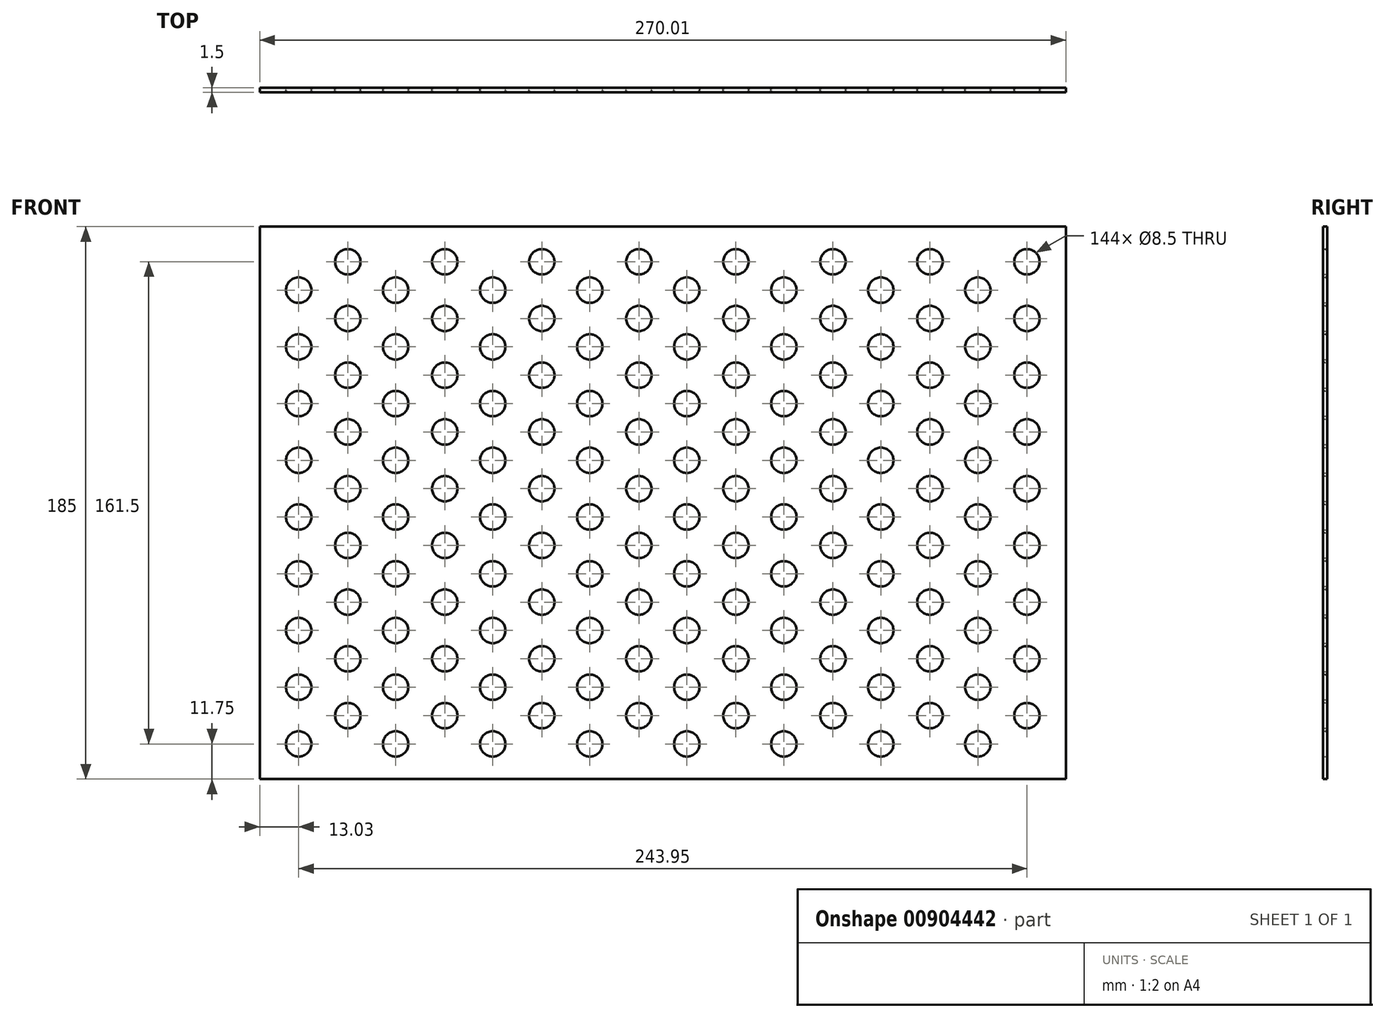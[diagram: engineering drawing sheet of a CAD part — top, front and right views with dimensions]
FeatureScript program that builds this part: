
annotation { "Feature Type Name" : "Feature", "Feature Type Description" : "" }
export const myFeature = defineFeature(function(context is Context, id is Id, definition is map)
    precondition{}
    {
        {
            var Q0;
            Q0=qCreatedBy(makeId("Front.planeOp"),FACE);
            var sketch = newSketch(context, id + "F0", { "sketchPlane" : qUnion([Q0])});
            skCircle(sketch, "E0", {"center": v(0, 0) * mm, "radius": 4.25 * mm});
            skCircle(sketch, "E1", {"center": v(16.45, 9.5) * mm, "radius": 4.25 * mm});
            skCircle(sketch, "E2.0.1.0", {"center": v(0, 19) * mm, "radius": 4.25 * mm});
            skCircle(sketch, "E2.0.1.1", {"center": v(16.45, 28.5) * mm, "radius": 4.25 * mm});
            skCircle(sketch, "E2.0.2.0", {"center": v(0, 38) * mm, "radius": 4.25 * mm});
            skCircle(sketch, "E2.0.2.1", {"center": v(16.45, 47.5) * mm, "radius": 4.25 * mm});
            skCircle(sketch, "E2.0.3.0", {"center": v(0, 57) * mm, "radius": 4.25 * mm});
            skCircle(sketch, "E2.0.3.1", {"center": v(16.45, 66.5) * mm, "radius": 4.25 * mm});
            skCircle(sketch, "E2.0.4.0", {"center": v(0, 76) * mm, "radius": 4.25 * mm});
            skCircle(sketch, "E2.0.4.1", {"center": v(16.45, 85.5) * mm, "radius": 4.25 * mm});
            skCircle(sketch, "E2.0.5.0", {"center": v(0, 95) * mm, "radius": 4.25 * mm});
            skCircle(sketch, "E2.0.5.1", {"center": v(16.45, 104.5) * mm, "radius": 4.25 * mm});
            skCircle(sketch, "E2.0.6.0", {"center": v(0, 114) * mm, "radius": 4.25 * mm});
            skCircle(sketch, "E2.0.6.1", {"center": v(16.45, 123.5) * mm, "radius": 4.25 * mm});
            skCircle(sketch, "E2.0.7.0", {"center": v(0, 133) * mm, "radius": 4.25 * mm});
            skCircle(sketch, "E2.0.7.1", {"center": v(16.45, 142.5) * mm, "radius": 4.25 * mm});
            skCircle(sketch, "E2.0.8.0", {"center": v(0, 152) * mm, "radius": 4.25 * mm});
            skCircle(sketch, "E2.0.8.1", {"center": v(16.45, 161.5) * mm, "radius": 4.25 * mm});
            skCircle(sketch, "E2.1.0.0", {"center": v(32.5, 0) * mm, "radius": 4.25 * mm});
            skCircle(sketch, "E2.1.0.1", {"center": v(48.95, 9.5) * mm, "radius": 4.25 * mm});
            skCircle(sketch, "E2.1.1.0", {"center": v(32.5, 19) * mm, "radius": 4.25 * mm});
            skCircle(sketch, "E2.1.1.1", {"center": v(48.95, 28.5) * mm, "radius": 4.25 * mm});
            skCircle(sketch, "E2.1.2.0", {"center": v(32.5, 38) * mm, "radius": 4.25 * mm});
            skCircle(sketch, "E2.1.2.1", {"center": v(48.95, 47.5) * mm, "radius": 4.25 * mm});
            skCircle(sketch, "E2.1.3.0", {"center": v(32.5, 57) * mm, "radius": 4.25 * mm});
            skCircle(sketch, "E2.1.3.1", {"center": v(48.95, 66.5) * mm, "radius": 4.25 * mm});
            skCircle(sketch, "E2.1.4.0", {"center": v(32.5, 76) * mm, "radius": 4.25 * mm});
            skCircle(sketch, "E2.1.4.1", {"center": v(48.95, 85.5) * mm, "radius": 4.25 * mm});
            skCircle(sketch, "E2.1.5.0", {"center": v(32.5, 95) * mm, "radius": 4.25 * mm});
            skCircle(sketch, "E2.1.5.1", {"center": v(48.95, 104.5) * mm, "radius": 4.25 * mm});
            skCircle(sketch, "E2.1.6.0", {"center": v(32.5, 114) * mm, "radius": 4.25 * mm});
            skCircle(sketch, "E2.1.6.1", {"center": v(48.95, 123.5) * mm, "radius": 4.25 * mm});
            skCircle(sketch, "E2.1.7.0", {"center": v(32.5, 133) * mm, "radius": 4.25 * mm});
            skCircle(sketch, "E2.1.7.1", {"center": v(48.95, 142.5) * mm, "radius": 4.25 * mm});
            skCircle(sketch, "E2.1.8.0", {"center": v(32.5, 152) * mm, "radius": 4.25 * mm});
            skCircle(sketch, "E2.1.8.1", {"center": v(48.95, 161.5) * mm, "radius": 4.25 * mm});
            skCircle(sketch, "E2.2.0.0", {"center": v(65, 0) * mm, "radius": 4.25 * mm});
            skCircle(sketch, "E2.2.0.1", {"center": v(81.45, 9.5) * mm, "radius": 4.25 * mm});
            skCircle(sketch, "E2.2.1.0", {"center": v(65, 19) * mm, "radius": 4.25 * mm});
            skCircle(sketch, "E2.2.1.1", {"center": v(81.45, 28.5) * mm, "radius": 4.25 * mm});
            skCircle(sketch, "E2.2.2.0", {"center": v(65, 38) * mm, "radius": 4.25 * mm});
            skCircle(sketch, "E2.2.2.1", {"center": v(81.45, 47.5) * mm, "radius": 4.25 * mm});
            skCircle(sketch, "E2.2.3.0", {"center": v(65, 57) * mm, "radius": 4.25 * mm});
            skCircle(sketch, "E2.2.3.1", {"center": v(81.45, 66.5) * mm, "radius": 4.25 * mm});
            skCircle(sketch, "E2.2.4.0", {"center": v(65, 76) * mm, "radius": 4.25 * mm});
            skCircle(sketch, "E2.2.4.1", {"center": v(81.45, 85.5) * mm, "radius": 4.25 * mm});
            skCircle(sketch, "E2.2.5.0", {"center": v(65, 95) * mm, "radius": 4.25 * mm});
            skCircle(sketch, "E2.2.5.1", {"center": v(81.45, 104.5) * mm, "radius": 4.25 * mm});
            skCircle(sketch, "E2.2.6.0", {"center": v(65, 114) * mm, "radius": 4.25 * mm});
            skCircle(sketch, "E2.2.6.1", {"center": v(81.45, 123.5) * mm, "radius": 4.25 * mm});
            skCircle(sketch, "E2.2.7.0", {"center": v(65, 133) * mm, "radius": 4.25 * mm});
            skCircle(sketch, "E2.2.7.1", {"center": v(81.45, 142.5) * mm, "radius": 4.25 * mm});
            skCircle(sketch, "E2.2.8.0", {"center": v(65, 152) * mm, "radius": 4.25 * mm});
            skCircle(sketch, "E2.2.8.1", {"center": v(81.45, 161.5) * mm, "radius": 4.25 * mm});
            skLineSegment(sketch, "E2.direction1", {"start": v(0, 0) * mm, "end": v(32.5, 0) * mm, "construction": true});
            skLineSegment(sketch, "E2.direction2", {"start": v(0, 0) * mm, "end": v(0, 19) * mm, "construction": true});
            skCircle(sketch, "E3.0.3.0", {"center": v(97.5, 0) * mm, "radius": 4.25 * mm});
            skCircle(sketch, "E3.2.3.0", {"center": v(113.95, 9.5) * mm, "radius": 4.25 * mm});
            skCircle(sketch, "E3.0.3.1", {"center": v(97.5, 19) * mm, "radius": 4.25 * mm});
            skCircle(sketch, "E3.2.3.1", {"center": v(113.95, 28.5) * mm, "radius": 4.25 * mm});
            skCircle(sketch, "E3.0.3.2", {"center": v(97.5, 38) * mm, "radius": 4.25 * mm});
            skCircle(sketch, "E3.2.3.2", {"center": v(113.95, 47.5) * mm, "radius": 4.25 * mm});
            skCircle(sketch, "E3.0.3.3", {"center": v(97.5, 57) * mm, "radius": 4.25 * mm});
            skCircle(sketch, "E3.2.3.3", {"center": v(113.95, 66.5) * mm, "radius": 4.25 * mm});
            skCircle(sketch, "E3.0.3.4", {"center": v(97.5, 76) * mm, "radius": 4.25 * mm});
            skCircle(sketch, "E3.2.3.4", {"center": v(113.95, 85.5) * mm, "radius": 4.25 * mm});
            skCircle(sketch, "E3.0.3.5", {"center": v(97.5, 95) * mm, "radius": 4.25 * mm});
            skCircle(sketch, "E3.2.3.5", {"center": v(113.95, 104.5) * mm, "radius": 4.25 * mm});
            skCircle(sketch, "E3.0.3.6", {"center": v(97.5, 114) * mm, "radius": 4.25 * mm});
            skCircle(sketch, "E3.2.3.6", {"center": v(113.95, 123.5) * mm, "radius": 4.25 * mm});
            skCircle(sketch, "E3.0.3.7", {"center": v(97.5, 133) * mm, "radius": 4.25 * mm});
            skCircle(sketch, "E3.2.3.7", {"center": v(113.95, 142.5) * mm, "radius": 4.25 * mm});
            skCircle(sketch, "E3.0.3.8", {"center": v(97.5, 152) * mm, "radius": 4.25 * mm});
            skCircle(sketch, "E3.2.3.8", {"center": v(113.95, 161.5) * mm, "radius": 4.25 * mm});
            skCircle(sketch, "E3.0.4.0", {"center": v(130, 0) * mm, "radius": 4.25 * mm});
            skCircle(sketch, "E3.2.4.0", {"center": v(146.45, 9.5) * mm, "radius": 4.25 * mm});
            skCircle(sketch, "E3.0.4.1", {"center": v(130, 19) * mm, "radius": 4.25 * mm});
            skCircle(sketch, "E3.2.4.1", {"center": v(146.45, 28.5) * mm, "radius": 4.25 * mm});
            skCircle(sketch, "E3.0.4.2", {"center": v(130, 38) * mm, "radius": 4.25 * mm});
            skCircle(sketch, "E3.2.4.2", {"center": v(146.45, 47.5) * mm, "radius": 4.25 * mm});
            skCircle(sketch, "E3.0.4.3", {"center": v(130, 57) * mm, "radius": 4.25 * mm});
            skCircle(sketch, "E3.2.4.3", {"center": v(146.45, 66.5) * mm, "radius": 4.25 * mm});
            skCircle(sketch, "E3.0.4.4", {"center": v(130, 76) * mm, "radius": 4.25 * mm});
            skCircle(sketch, "E3.2.4.4", {"center": v(146.45, 85.5) * mm, "radius": 4.25 * mm});
            skCircle(sketch, "E3.0.4.5", {"center": v(130, 95) * mm, "radius": 4.25 * mm});
            skCircle(sketch, "E3.2.4.5", {"center": v(146.45, 104.5) * mm, "radius": 4.25 * mm});
            skCircle(sketch, "E3.0.4.6", {"center": v(130, 114) * mm, "radius": 4.25 * mm});
            skCircle(sketch, "E3.2.4.6", {"center": v(146.45, 123.5) * mm, "radius": 4.25 * mm});
            skCircle(sketch, "E3.0.4.7", {"center": v(130, 133) * mm, "radius": 4.25 * mm});
            skCircle(sketch, "E3.2.4.7", {"center": v(146.45, 142.5) * mm, "radius": 4.25 * mm});
            skCircle(sketch, "E3.0.4.8", {"center": v(130, 152) * mm, "radius": 4.25 * mm});
            skCircle(sketch, "E3.2.4.8", {"center": v(146.45, 161.5) * mm, "radius": 4.25 * mm});
            skCircle(sketch, "E3.0.5.0", {"center": v(162.5, 0) * mm, "radius": 4.25 * mm});
            skCircle(sketch, "E3.2.5.0", {"center": v(178.95, 9.5) * mm, "radius": 4.25 * mm});
            skCircle(sketch, "E3.0.5.1", {"center": v(162.5, 19) * mm, "radius": 4.25 * mm});
            skCircle(sketch, "E3.2.5.1", {"center": v(178.95, 28.5) * mm, "radius": 4.25 * mm});
            skCircle(sketch, "E3.0.5.2", {"center": v(162.5, 38) * mm, "radius": 4.25 * mm});
            skCircle(sketch, "E3.2.5.2", {"center": v(178.95, 47.5) * mm, "radius": 4.25 * mm});
            skCircle(sketch, "E3.0.5.3", {"center": v(162.5, 57) * mm, "radius": 4.25 * mm});
            skCircle(sketch, "E3.2.5.3", {"center": v(178.95, 66.5) * mm, "radius": 4.25 * mm});
            skCircle(sketch, "E3.0.5.4", {"center": v(162.5, 76) * mm, "radius": 4.25 * mm});
            skCircle(sketch, "E3.2.5.4", {"center": v(178.95, 85.5) * mm, "radius": 4.25 * mm});
            skCircle(sketch, "E3.0.5.5", {"center": v(162.5, 95) * mm, "radius": 4.25 * mm});
            skCircle(sketch, "E3.2.5.5", {"center": v(178.95, 104.5) * mm, "radius": 4.25 * mm});
            skCircle(sketch, "E3.0.5.6", {"center": v(162.5, 114) * mm, "radius": 4.25 * mm});
            skCircle(sketch, "E3.2.5.6", {"center": v(178.95, 123.5) * mm, "radius": 4.25 * mm});
            skCircle(sketch, "E3.0.5.7", {"center": v(162.5, 133) * mm, "radius": 4.25 * mm});
            skCircle(sketch, "E3.2.5.7", {"center": v(178.95, 142.5) * mm, "radius": 4.25 * mm});
            skCircle(sketch, "E3.0.5.8", {"center": v(162.5, 152) * mm, "radius": 4.25 * mm});
            skCircle(sketch, "E3.2.5.8", {"center": v(178.95, 161.5) * mm, "radius": 4.25 * mm});
            skCircle(sketch, "E3.0.6.0", {"center": v(195, 0) * mm, "radius": 4.25 * mm});
            skCircle(sketch, "E3.2.6.0", {"center": v(211.45, 9.5) * mm, "radius": 4.25 * mm});
            skCircle(sketch, "E3.0.6.1", {"center": v(195, 19) * mm, "radius": 4.25 * mm});
            skCircle(sketch, "E3.2.6.1", {"center": v(211.45, 28.5) * mm, "radius": 4.25 * mm});
            skCircle(sketch, "E3.0.6.2", {"center": v(195, 38) * mm, "radius": 4.25 * mm});
            skCircle(sketch, "E3.2.6.2", {"center": v(211.45, 47.5) * mm, "radius": 4.25 * mm});
            skCircle(sketch, "E3.0.6.3", {"center": v(195, 57) * mm, "radius": 4.25 * mm});
            skCircle(sketch, "E3.2.6.3", {"center": v(211.45, 66.5) * mm, "radius": 4.25 * mm});
            skCircle(sketch, "E3.0.6.4", {"center": v(195, 76) * mm, "radius": 4.25 * mm});
            skCircle(sketch, "E3.2.6.4", {"center": v(211.45, 85.5) * mm, "radius": 4.25 * mm});
            skCircle(sketch, "E3.0.6.5", {"center": v(195, 95) * mm, "radius": 4.25 * mm});
            skCircle(sketch, "E3.2.6.5", {"center": v(211.45, 104.5) * mm, "radius": 4.25 * mm});
            skCircle(sketch, "E3.0.6.6", {"center": v(195, 114) * mm, "radius": 4.25 * mm});
            skCircle(sketch, "E3.2.6.6", {"center": v(211.45, 123.5) * mm, "radius": 4.25 * mm});
            skCircle(sketch, "E3.0.6.7", {"center": v(195, 133) * mm, "radius": 4.25 * mm});
            skCircle(sketch, "E3.2.6.7", {"center": v(211.45, 142.5) * mm, "radius": 4.25 * mm});
            skCircle(sketch, "E3.0.6.8", {"center": v(195, 152) * mm, "radius": 4.25 * mm});
            skCircle(sketch, "E3.2.6.8", {"center": v(211.45, 161.5) * mm, "radius": 4.25 * mm});
            skCircle(sketch, "E3.0.7.0", {"center": v(227.5, 0) * mm, "radius": 4.25 * mm});
            skCircle(sketch, "E3.2.7.0", {"center": v(243.95, 9.5) * mm, "radius": 4.25 * mm});
            skCircle(sketch, "E3.0.7.1", {"center": v(227.5, 19) * mm, "radius": 4.25 * mm});
            skCircle(sketch, "E3.2.7.1", {"center": v(243.95, 28.5) * mm, "radius": 4.25 * mm});
            skCircle(sketch, "E3.0.7.2", {"center": v(227.5, 38) * mm, "radius": 4.25 * mm});
            skCircle(sketch, "E3.2.7.2", {"center": v(243.95, 47.5) * mm, "radius": 4.25 * mm});
            skCircle(sketch, "E3.0.7.3", {"center": v(227.5, 57) * mm, "radius": 4.25 * mm});
            skCircle(sketch, "E3.2.7.3", {"center": v(243.95, 66.5) * mm, "radius": 4.25 * mm});
            skCircle(sketch, "E3.0.7.4", {"center": v(227.5, 76) * mm, "radius": 4.25 * mm});
            skCircle(sketch, "E3.2.7.4", {"center": v(243.95, 85.5) * mm, "radius": 4.25 * mm});
            skCircle(sketch, "E3.0.7.5", {"center": v(227.5, 95) * mm, "radius": 4.25 * mm});
            skCircle(sketch, "E3.2.7.5", {"center": v(243.95, 104.5) * mm, "radius": 4.25 * mm});
            skCircle(sketch, "E3.0.7.6", {"center": v(227.5, 114) * mm, "radius": 4.25 * mm});
            skCircle(sketch, "E3.2.7.6", {"center": v(243.95, 123.5) * mm, "radius": 4.25 * mm});
            skCircle(sketch, "E3.0.7.7", {"center": v(227.5, 133) * mm, "radius": 4.25 * mm});
            skCircle(sketch, "E3.2.7.7", {"center": v(243.95, 142.5) * mm, "radius": 4.25 * mm});
            skCircle(sketch, "E3.0.7.8", {"center": v(227.5, 152) * mm, "radius": 4.25 * mm});
            skCircle(sketch, "E3.2.7.8", {"center": v(243.95, 161.5) * mm, "radius": 4.25 * mm});
            skLineSegment(sketch, "E4.bottom", {"start": v(-13.03, -11.75) * mm, "end": v(256.98, -11.75) * mm});
            skLineSegment(sketch, "E4.top", {"start": v(-13.03, 173.25) * mm, "end": v(256.98, 173.25) * mm});
            skLineSegment(sketch, "E4.left", {"start": v(-13.02, -11.75) * mm, "end": v(-13.03, 173.25) * mm});
            skLineSegment(sketch, "E4.right", {"start": v(256.98, -11.75) * mm, "end": v(256.98, 173.25) * mm});
            skSolve(sketch);
        }
        {
            var Q0;
            Q0=makeQuery(id+"F0.imprint","IMPRINT",FACE,{"disambiguationData":[TD([[makeQuery(id+"F0.imprint","IMPRINT",EDGE,{"derivedFrom":sQuery(id+"F0.wireOp",EDGE,"E0")}),-1.0]])]});
            extrude(context, id + "F1", {"entities" : qUnion([Q0]), "depth" : 1.5 * mm, "offsetDistance" : 25 * mm});
        }
        {
            var Q0;
            Q0=makeQuery(id+"F1.opExtrude","CAP_EDGE",EDGE,{"disambiguationData":[OSD([sQuery(id+"F0.wireOp",EDGE,"E2.0.6.1")])],"isStart":false});
            var Q1;
            Q1=makeQuery(id+"F1.opExtrude","CAP_EDGE",EDGE,{"disambiguationData":[OSD([sQuery(id+"F0.wireOp",EDGE,"E2.0.2.0")])],"isStart":false});
            var Q2;
            Q2=makeQuery(id+"F1.opExtrude","CAP_EDGE",EDGE,{"disambiguationData":[OSD([sQuery(id+"F0.wireOp",EDGE,"E2.0.2.1")])],"isStart":false});
            var Q3;
            Q3=makeQuery(id+"F1.opExtrude","CAP_EDGE",EDGE,{"disambiguationData":[OSD([sQuery(id+"F0.wireOp",EDGE,"E2.1.6.1")])],"isStart":false});
            var Q4;
            Q4=makeQuery(id+"F1.opExtrude","CAP_EDGE",EDGE,{"disambiguationData":[OSD([sQuery(id+"F0.wireOp",EDGE,"E1")])],"isStart":false});
            var Q5;
            Q5=makeQuery(id+"F1.opExtrude","CAP_EDGE",EDGE,{"disambiguationData":[OSD([sQuery(id+"F0.wireOp",EDGE,"E2.0.1.0")])],"isStart":false});
            var Q6;
            Q6=makeQuery(id+"F1.opExtrude","CAP_EDGE",EDGE,{"disambiguationData":[OSD([sQuery(id+"F0.wireOp",EDGE,"E2.0.1.1")])],"isStart":false});
            var Q7;
            Q7=makeQuery(id+"F1.opExtrude","CAP_EDGE",EDGE,{"disambiguationData":[OSD([sQuery(id+"F0.wireOp",EDGE,"E2.0.6.0")])],"isStart":false});
            var Q8;
            Q8=makeQuery(id+"F1.opExtrude","CAP_EDGE",EDGE,{"disambiguationData":[OSD([sQuery(id+"F0.wireOp",EDGE,"E2.1.1.0")])],"isStart":false});
            var Q9;
            Q9=makeQuery(id+"F1.opExtrude","CAP_EDGE",EDGE,{"disambiguationData":[OSD([sQuery(id+"F0.wireOp",EDGE,"E2.1.5.0")])],"isStart":false});
            var Q10;
            Q10=makeQuery(id+"F1.opExtrude","CAP_EDGE",EDGE,{"disambiguationData":[OSD([sQuery(id+"F0.wireOp",EDGE,"E2.2.0.0")])],"isStart":false});
            var Q11;
            Q11=makeQuery(id+"F1.opExtrude","CAP_EDGE",EDGE,{"disambiguationData":[OSD([sQuery(id+"F0.wireOp",EDGE,"E2.2.4.0")])],"isStart":false});
            var Q12;
            Q12=makeQuery(id+"F1.opExtrude","CAP_EDGE",EDGE,{"disambiguationData":[OSD([sQuery(id+"F0.wireOp",EDGE,"E2.2.8.0")])],"isStart":false});
            var Q13;
            Q13=makeQuery(id+"F1.opExtrude","CAP_EDGE",EDGE,{"disambiguationData":[OSD([sQuery(id+"F0.wireOp",EDGE,"E3.0.3.3")])],"isStart":false});
            var Q14;
            Q14=makeQuery(id+"F1.opExtrude","CAP_EDGE",EDGE,{"disambiguationData":[OSD([sQuery(id+"F0.wireOp",EDGE,"E3.0.3.7")])],"isStart":false});
            var Q15;
            Q15=makeQuery(id+"F1.opExtrude","CAP_EDGE",EDGE,{"disambiguationData":[OSD([sQuery(id+"F0.wireOp",EDGE,"E3.0.4.2")])],"isStart":false});
            var Q16;
            Q16=makeQuery(id+"F1.opExtrude","CAP_EDGE",EDGE,{"disambiguationData":[OSD([sQuery(id+"F0.wireOp",EDGE,"E3.0.4.6")])],"isStart":false});
            var Q17;
            Q17=makeQuery(id+"F1.opExtrude","CAP_EDGE",EDGE,{"disambiguationData":[OSD([sQuery(id+"F0.wireOp",EDGE,"E3.0.5.1")])],"isStart":false});
            var Q18;
            Q18=makeQuery(id+"F1.opExtrude","CAP_EDGE",EDGE,{"disambiguationData":[OSD([sQuery(id+"F0.wireOp",EDGE,"E3.0.5.5")])],"isStart":false});
            var Q19;
            Q19=makeQuery(id+"F1.opExtrude","CAP_EDGE",EDGE,{"disambiguationData":[OSD([sQuery(id+"F0.wireOp",EDGE,"E3.0.6.0")])],"isStart":false});
            var Q20;
            Q20=makeQuery(id+"F1.opExtrude","CAP_EDGE",EDGE,{"disambiguationData":[OSD([sQuery(id+"F0.wireOp",EDGE,"E3.0.6.4")])],"isStart":false});
            var Q21;
            Q21=makeQuery(id+"F1.opExtrude","CAP_EDGE",EDGE,{"disambiguationData":[OSD([sQuery(id+"F0.wireOp",EDGE,"E3.0.6.8")])],"isStart":false});
            var Q22;
            Q22=makeQuery(id+"F1.opExtrude","CAP_EDGE",EDGE,{"disambiguationData":[OSD([sQuery(id+"F0.wireOp",EDGE,"E3.0.7.3")])],"isStart":false});
            var Q23;
            Q23=makeQuery(id+"F1.opExtrude","CAP_EDGE",EDGE,{"disambiguationData":[OSD([sQuery(id+"F0.wireOp",EDGE,"E3.0.7.7")])],"isStart":false});
            var Q24;
            Q24=makeQuery(id+"F1.opExtrude","CAP_EDGE",EDGE,{"disambiguationData":[OSD([sQuery(id+"F0.wireOp",EDGE,"E2.2.6.1")])],"isStart":false});
            var Q25;
            Q25=makeQuery(id+"F1.opExtrude","CAP_EDGE",EDGE,{"disambiguationData":[OSD([sQuery(id+"F0.wireOp",EDGE,"E2.1.1.1")])],"isStart":false});
            var Q26;
            Q26=makeQuery(id+"F1.opExtrude","CAP_EDGE",EDGE,{"disambiguationData":[OSD([sQuery(id+"F0.wireOp",EDGE,"E2.1.5.1")])],"isStart":false});
            var Q27;
            Q27=makeQuery(id+"F1.opExtrude","CAP_EDGE",EDGE,{"disambiguationData":[OSD([sQuery(id+"F0.wireOp",EDGE,"E2.2.0.1")])],"isStart":false});
            var Q28;
            Q28=makeQuery(id+"F1.opExtrude","CAP_EDGE",EDGE,{"disambiguationData":[OSD([sQuery(id+"F0.wireOp",EDGE,"E2.2.4.1")])],"isStart":false});
            var Q29;
            Q29=makeQuery(id+"F1.opExtrude","CAP_EDGE",EDGE,{"disambiguationData":[OSD([sQuery(id+"F0.wireOp",EDGE,"E2.2.8.1")])],"isStart":false});
            var Q30;
            Q30=makeQuery(id+"F1.opExtrude","CAP_EDGE",EDGE,{"disambiguationData":[OSD([sQuery(id+"F0.wireOp",EDGE,"E3.2.3.3")])],"isStart":false});
            var Q31;
            Q31=makeQuery(id+"F1.opExtrude","CAP_EDGE",EDGE,{"disambiguationData":[OSD([sQuery(id+"F0.wireOp",EDGE,"E3.2.3.7")])],"isStart":false});
            var Q32;
            Q32=makeQuery(id+"F1.opExtrude","CAP_EDGE",EDGE,{"disambiguationData":[OSD([sQuery(id+"F0.wireOp",EDGE,"E3.2.4.2")])],"isStart":false});
            var Q33;
            Q33=makeQuery(id+"F1.opExtrude","CAP_EDGE",EDGE,{"disambiguationData":[OSD([sQuery(id+"F0.wireOp",EDGE,"E3.2.4.6")])],"isStart":false});
            var Q34;
            Q34=makeQuery(id+"F1.opExtrude","CAP_EDGE",EDGE,{"disambiguationData":[OSD([sQuery(id+"F0.wireOp",EDGE,"E3.2.5.1")])],"isStart":false});
            var Q35;
            Q35=makeQuery(id+"F1.opExtrude","CAP_EDGE",EDGE,{"disambiguationData":[OSD([sQuery(id+"F0.wireOp",EDGE,"E3.2.5.5")])],"isStart":false});
            var Q36;
            Q36=makeQuery(id+"F1.opExtrude","CAP_EDGE",EDGE,{"disambiguationData":[OSD([sQuery(id+"F0.wireOp",EDGE,"E3.2.6.0")])],"isStart":false});
            var Q37;
            Q37=makeQuery(id+"F1.opExtrude","CAP_EDGE",EDGE,{"disambiguationData":[OSD([sQuery(id+"F0.wireOp",EDGE,"E3.2.6.4")])],"isStart":false});
            var Q38;
            Q38=makeQuery(id+"F1.opExtrude","CAP_EDGE",EDGE,{"disambiguationData":[OSD([sQuery(id+"F0.wireOp",EDGE,"E3.2.6.8")])],"isStart":false});
            var Q39;
            Q39=makeQuery(id+"F1.opExtrude","CAP_EDGE",EDGE,{"disambiguationData":[OSD([sQuery(id+"F0.wireOp",EDGE,"E3.2.7.3")])],"isStart":false});
            var Q40;
            Q40=makeQuery(id+"F1.opExtrude","CAP_EDGE",EDGE,{"disambiguationData":[OSD([sQuery(id+"F0.wireOp",EDGE,"E3.2.7.7")])],"isStart":false});
            var Q41;
            Q41=makeQuery(id+"F1.opExtrude","CAP_EDGE",EDGE,{"disambiguationData":[OSD([sQuery(id+"F0.wireOp",EDGE,"E2.0.3.0")])],"isStart":false});
            var Q42;
            Q42=makeQuery(id+"F1.opExtrude","CAP_EDGE",EDGE,{"disambiguationData":[OSD([sQuery(id+"F0.wireOp",EDGE,"E2.0.7.0")])],"isStart":false});
            var Q43;
            Q43=makeQuery(id+"F1.opExtrude","CAP_EDGE",EDGE,{"disambiguationData":[OSD([sQuery(id+"F0.wireOp",EDGE,"E2.1.2.0")])],"isStart":false});
            var Q44;
            Q44=makeQuery(id+"F1.opExtrude","CAP_EDGE",EDGE,{"disambiguationData":[OSD([sQuery(id+"F0.wireOp",EDGE,"E2.1.6.0")])],"isStart":false});
            var Q45;
            Q45=makeQuery(id+"F1.opExtrude","CAP_EDGE",EDGE,{"disambiguationData":[OSD([sQuery(id+"F0.wireOp",EDGE,"E2.2.1.0")])],"isStart":false});
            var Q46;
            Q46=makeQuery(id+"F1.opExtrude","CAP_EDGE",EDGE,{"disambiguationData":[OSD([sQuery(id+"F0.wireOp",EDGE,"E2.2.5.0")])],"isStart":false});
            var Q47;
            Q47=makeQuery(id+"F1.opExtrude","CAP_EDGE",EDGE,{"disambiguationData":[OSD([sQuery(id+"F0.wireOp",EDGE,"E3.0.3.0")])],"isStart":false});
            var Q48;
            Q48=makeQuery(id+"F1.opExtrude","CAP_EDGE",EDGE,{"disambiguationData":[OSD([sQuery(id+"F0.wireOp",EDGE,"E3.0.3.4")])],"isStart":false});
            var Q49;
            Q49=makeQuery(id+"F1.opExtrude","CAP_EDGE",EDGE,{"disambiguationData":[OSD([sQuery(id+"F0.wireOp",EDGE,"E3.0.3.8")])],"isStart":false});
            var Q50;
            Q50=makeQuery(id+"F1.opExtrude","CAP_EDGE",EDGE,{"disambiguationData":[OSD([sQuery(id+"F0.wireOp",EDGE,"E3.0.4.3")])],"isStart":false});
            var Q51;
            Q51=makeQuery(id+"F1.opExtrude","CAP_EDGE",EDGE,{"disambiguationData":[OSD([sQuery(id+"F0.wireOp",EDGE,"E3.0.4.7")])],"isStart":false});
            var Q52;
            Q52=makeQuery(id+"F1.opExtrude","CAP_EDGE",EDGE,{"disambiguationData":[OSD([sQuery(id+"F0.wireOp",EDGE,"E3.0.5.2")])],"isStart":false});
            var Q53;
            Q53=makeQuery(id+"F1.opExtrude","CAP_EDGE",EDGE,{"disambiguationData":[OSD([sQuery(id+"F0.wireOp",EDGE,"E3.0.5.6")])],"isStart":false});
            var Q54;
            Q54=makeQuery(id+"F1.opExtrude","CAP_EDGE",EDGE,{"disambiguationData":[OSD([sQuery(id+"F0.wireOp",EDGE,"E3.0.6.1")])],"isStart":false});
            var Q55;
            Q55=makeQuery(id+"F1.opExtrude","CAP_EDGE",EDGE,{"disambiguationData":[OSD([sQuery(id+"F0.wireOp",EDGE,"E3.0.6.5")])],"isStart":false});
            var Q56;
            Q56=makeQuery(id+"F1.opExtrude","CAP_EDGE",EDGE,{"disambiguationData":[OSD([sQuery(id+"F0.wireOp",EDGE,"E3.0.7.0")])],"isStart":false});
            var Q57;
            Q57=makeQuery(id+"F1.opExtrude","CAP_EDGE",EDGE,{"disambiguationData":[OSD([sQuery(id+"F0.wireOp",EDGE,"E3.0.7.4")])],"isStart":false});
            var Q58;
            Q58=makeQuery(id+"F1.opExtrude","CAP_EDGE",EDGE,{"disambiguationData":[OSD([sQuery(id+"F0.wireOp",EDGE,"E3.0.7.8")])],"isStart":false});
            var Q59;
            Q59=makeQuery(id+"F1.opExtrude","CAP_EDGE",EDGE,{"disambiguationData":[OSD([sQuery(id+"F0.wireOp",EDGE,"E2.0.3.1")])],"isStart":false});
            var Q60;
            Q60=makeQuery(id+"F1.opExtrude","CAP_EDGE",EDGE,{"disambiguationData":[OSD([sQuery(id+"F0.wireOp",EDGE,"E2.0.7.1")])],"isStart":false});
            var Q61;
            Q61=makeQuery(id+"F1.opExtrude","CAP_EDGE",EDGE,{"disambiguationData":[OSD([sQuery(id+"F0.wireOp",EDGE,"E2.1.2.1")])],"isStart":false});
            var Q62;
            Q62=makeQuery(id+"F1.opExtrude","CAP_EDGE",EDGE,{"disambiguationData":[OSD([sQuery(id+"F0.wireOp",EDGE,"E2.2.1.1")])],"isStart":false});
            var Q63;
            Q63=makeQuery(id+"F1.opExtrude","CAP_EDGE",EDGE,{"disambiguationData":[OSD([sQuery(id+"F0.wireOp",EDGE,"E2.2.5.1")])],"isStart":false});
            var Q64;
            Q64=makeQuery(id+"F1.opExtrude","CAP_EDGE",EDGE,{"disambiguationData":[OSD([sQuery(id+"F0.wireOp",EDGE,"E3.2.3.0")])],"isStart":false});
            var Q65;
            Q65=makeQuery(id+"F1.opExtrude","CAP_EDGE",EDGE,{"disambiguationData":[OSD([sQuery(id+"F0.wireOp",EDGE,"E3.2.3.4")])],"isStart":false});
            var Q66;
            Q66=makeQuery(id+"F1.opExtrude","CAP_EDGE",EDGE,{"disambiguationData":[OSD([sQuery(id+"F0.wireOp",EDGE,"E3.2.3.8")])],"isStart":false});
            var Q67;
            Q67=makeQuery(id+"F1.opExtrude","CAP_EDGE",EDGE,{"disambiguationData":[OSD([sQuery(id+"F0.wireOp",EDGE,"E3.2.4.3")])],"isStart":false});
            var Q68;
            Q68=makeQuery(id+"F1.opExtrude","CAP_EDGE",EDGE,{"disambiguationData":[OSD([sQuery(id+"F0.wireOp",EDGE,"E3.2.4.7")])],"isStart":false});
            var Q69;
            Q69=makeQuery(id+"F1.opExtrude","CAP_EDGE",EDGE,{"disambiguationData":[OSD([sQuery(id+"F0.wireOp",EDGE,"E3.2.5.2")])],"isStart":false});
            var Q70;
            Q70=makeQuery(id+"F1.opExtrude","CAP_EDGE",EDGE,{"disambiguationData":[OSD([sQuery(id+"F0.wireOp",EDGE,"E3.2.5.6")])],"isStart":false});
            var Q71;
            Q71=makeQuery(id+"F1.opExtrude","CAP_EDGE",EDGE,{"disambiguationData":[OSD([sQuery(id+"F0.wireOp",EDGE,"E3.2.6.1")])],"isStart":false});
            var Q72;
            Q72=makeQuery(id+"F1.opExtrude","CAP_EDGE",EDGE,{"disambiguationData":[OSD([sQuery(id+"F0.wireOp",EDGE,"E3.2.6.5")])],"isStart":false});
            var Q73;
            Q73=makeQuery(id+"F1.opExtrude","CAP_EDGE",EDGE,{"disambiguationData":[OSD([sQuery(id+"F0.wireOp",EDGE,"E3.2.7.0")])],"isStart":false});
            var Q74;
            Q74=makeQuery(id+"F1.opExtrude","CAP_EDGE",EDGE,{"disambiguationData":[OSD([sQuery(id+"F0.wireOp",EDGE,"E3.2.7.4")])],"isStart":false});
            var Q75;
            Q75=makeQuery(id+"F1.opExtrude","CAP_EDGE",EDGE,{"disambiguationData":[OSD([sQuery(id+"F0.wireOp",EDGE,"E3.2.7.8")])],"isStart":false});
            var Q76;
            Q76=makeQuery(id+"F1.opExtrude","CAP_EDGE",EDGE,{"disambiguationData":[OSD([sQuery(id+"F0.wireOp",EDGE,"E2.0.4.0")])],"isStart":false});
            var Q77;
            Q77=makeQuery(id+"F1.opExtrude","CAP_EDGE",EDGE,{"disambiguationData":[OSD([sQuery(id+"F0.wireOp",EDGE,"E2.0.8.0")])],"isStart":false});
            var Q78;
            Q78=makeQuery(id+"F1.opExtrude","CAP_EDGE",EDGE,{"disambiguationData":[OSD([sQuery(id+"F0.wireOp",EDGE,"E2.1.3.0")])],"isStart":false});
            var Q79;
            Q79=makeQuery(id+"F1.opExtrude","CAP_EDGE",EDGE,{"disambiguationData":[OSD([sQuery(id+"F0.wireOp",EDGE,"E2.1.7.0")])],"isStart":false});
            var Q80;
            Q80=makeQuery(id+"F1.opExtrude","CAP_EDGE",EDGE,{"disambiguationData":[OSD([sQuery(id+"F0.wireOp",EDGE,"E2.2.2.0")])],"isStart":false});
            var Q81;
            Q81=makeQuery(id+"F1.opExtrude","CAP_EDGE",EDGE,{"disambiguationData":[OSD([sQuery(id+"F0.wireOp",EDGE,"E2.2.6.0")])],"isStart":false});
            var Q82;
            Q82=makeQuery(id+"F1.opExtrude","CAP_EDGE",EDGE,{"disambiguationData":[OSD([sQuery(id+"F0.wireOp",EDGE,"E3.0.3.1")])],"isStart":false});
            var Q83;
            Q83=makeQuery(id+"F1.opExtrude","CAP_EDGE",EDGE,{"disambiguationData":[OSD([sQuery(id+"F0.wireOp",EDGE,"E3.0.3.5")])],"isStart":false});
            var Q84;
            Q84=makeQuery(id+"F1.opExtrude","CAP_EDGE",EDGE,{"disambiguationData":[OSD([sQuery(id+"F0.wireOp",EDGE,"E3.0.4.0")])],"isStart":false});
            var Q85;
            Q85=makeQuery(id+"F1.opExtrude","CAP_EDGE",EDGE,{"disambiguationData":[OSD([sQuery(id+"F0.wireOp",EDGE,"E3.0.4.4")])],"isStart":false});
            var Q86;
            Q86=makeQuery(id+"F1.opExtrude","CAP_EDGE",EDGE,{"disambiguationData":[OSD([sQuery(id+"F0.wireOp",EDGE,"E3.0.4.8")])],"isStart":false});
            var Q87;
            Q87=makeQuery(id+"F1.opExtrude","CAP_EDGE",EDGE,{"disambiguationData":[OSD([sQuery(id+"F0.wireOp",EDGE,"E3.0.5.3")])],"isStart":false});
            var Q88;
            Q88=makeQuery(id+"F1.opExtrude","CAP_EDGE",EDGE,{"disambiguationData":[OSD([sQuery(id+"F0.wireOp",EDGE,"E3.0.5.7")])],"isStart":false});
            var Q89;
            Q89=makeQuery(id+"F1.opExtrude","CAP_EDGE",EDGE,{"disambiguationData":[OSD([sQuery(id+"F0.wireOp",EDGE,"E3.0.6.2")])],"isStart":false});
            var Q90;
            Q90=makeQuery(id+"F1.opExtrude","CAP_EDGE",EDGE,{"disambiguationData":[OSD([sQuery(id+"F0.wireOp",EDGE,"E3.0.6.6")])],"isStart":false});
            var Q91;
            Q91=makeQuery(id+"F1.opExtrude","CAP_EDGE",EDGE,{"disambiguationData":[OSD([sQuery(id+"F0.wireOp",EDGE,"E3.0.7.1")])],"isStart":false});
            var Q92;
            Q92=makeQuery(id+"F1.opExtrude","CAP_EDGE",EDGE,{"disambiguationData":[OSD([sQuery(id+"F0.wireOp",EDGE,"E3.0.7.5")])],"isStart":false});
            var Q93;
            Q93=makeQuery(id+"F1.opExtrude","CAP_EDGE",EDGE,{"disambiguationData":[OSD([sQuery(id+"F0.wireOp",EDGE,"E2.0.4.1")])],"isStart":false});
            var Q94;
            Q94=makeQuery(id+"F1.opExtrude","CAP_EDGE",EDGE,{"disambiguationData":[OSD([sQuery(id+"F0.wireOp",EDGE,"E2.0.8.1")])],"isStart":false});
            var Q95;
            Q95=makeQuery(id+"F1.opExtrude","CAP_EDGE",EDGE,{"disambiguationData":[OSD([sQuery(id+"F0.wireOp",EDGE,"E2.1.3.1")])],"isStart":false});
            var Q96;
            Q96=makeQuery(id+"F1.opExtrude","CAP_EDGE",EDGE,{"disambiguationData":[OSD([sQuery(id+"F0.wireOp",EDGE,"E2.1.7.1")])],"isStart":false});
            var Q97;
            Q97=makeQuery(id+"F1.opExtrude","CAP_EDGE",EDGE,{"disambiguationData":[OSD([sQuery(id+"F0.wireOp",EDGE,"E2.2.2.1")])],"isStart":false});
            var Q98;
            Q98=makeQuery(id+"F1.opExtrude","CAP_EDGE",EDGE,{"disambiguationData":[OSD([sQuery(id+"F0.wireOp",EDGE,"E3.2.3.1")])],"isStart":false});
            var Q99;
            Q99=makeQuery(id+"F1.opExtrude","CAP_EDGE",EDGE,{"disambiguationData":[OSD([sQuery(id+"F0.wireOp",EDGE,"E3.2.3.5")])],"isStart":false});
            var Q100;
            Q100=makeQuery(id+"F1.opExtrude","CAP_EDGE",EDGE,{"disambiguationData":[OSD([sQuery(id+"F0.wireOp",EDGE,"E3.2.4.0")])],"isStart":false});
            var Q101;
            Q101=makeQuery(id+"F1.opExtrude","CAP_EDGE",EDGE,{"disambiguationData":[OSD([sQuery(id+"F0.wireOp",EDGE,"E3.2.4.4")])],"isStart":false});
            var Q102;
            Q102=makeQuery(id+"F1.opExtrude","CAP_EDGE",EDGE,{"disambiguationData":[OSD([sQuery(id+"F0.wireOp",EDGE,"E3.2.4.8")])],"isStart":false});
            var Q103;
            Q103=makeQuery(id+"F1.opExtrude","CAP_EDGE",EDGE,{"disambiguationData":[OSD([sQuery(id+"F0.wireOp",EDGE,"E3.2.5.3")])],"isStart":false});
            var Q104;
            Q104=makeQuery(id+"F1.opExtrude","CAP_EDGE",EDGE,{"disambiguationData":[OSD([sQuery(id+"F0.wireOp",EDGE,"E3.2.5.7")])],"isStart":false});
            var Q105;
            Q105=makeQuery(id+"F1.opExtrude","CAP_EDGE",EDGE,{"disambiguationData":[OSD([sQuery(id+"F0.wireOp",EDGE,"E3.2.6.2")])],"isStart":false});
            var Q106;
            Q106=makeQuery(id+"F1.opExtrude","CAP_EDGE",EDGE,{"disambiguationData":[OSD([sQuery(id+"F0.wireOp",EDGE,"E3.2.6.6")])],"isStart":false});
            var Q107;
            Q107=makeQuery(id+"F1.opExtrude","CAP_EDGE",EDGE,{"disambiguationData":[OSD([sQuery(id+"F0.wireOp",EDGE,"E3.2.7.1")])],"isStart":false});
            var Q108;
            Q108=makeQuery(id+"F1.opExtrude","CAP_EDGE",EDGE,{"disambiguationData":[OSD([sQuery(id+"F0.wireOp",EDGE,"E3.2.7.5")])],"isStart":false});
            var Q109;
            Q109=makeQuery(id+"F1.opExtrude","CAP_EDGE",EDGE,{"disambiguationData":[OSD([sQuery(id+"F0.wireOp",EDGE,"E2.0.5.0")])],"isStart":false});
            var Q110;
            Q110=makeQuery(id+"F1.opExtrude","CAP_EDGE",EDGE,{"disambiguationData":[OSD([sQuery(id+"F0.wireOp",EDGE,"E2.1.0.0")])],"isStart":false});
            var Q111;
            Q111=makeQuery(id+"F1.opExtrude","CAP_EDGE",EDGE,{"disambiguationData":[OSD([sQuery(id+"F0.wireOp",EDGE,"E2.1.4.0")])],"isStart":false});
            var Q112;
            Q112=makeQuery(id+"F1.opExtrude","CAP_EDGE",EDGE,{"disambiguationData":[OSD([sQuery(id+"F0.wireOp",EDGE,"E2.1.8.0")])],"isStart":false});
            var Q113;
            Q113=makeQuery(id+"F1.opExtrude","CAP_EDGE",EDGE,{"disambiguationData":[OSD([sQuery(id+"F0.wireOp",EDGE,"E2.2.3.0")])],"isStart":false});
            var Q114;
            Q114=makeQuery(id+"F1.opExtrude","CAP_EDGE",EDGE,{"disambiguationData":[OSD([sQuery(id+"F0.wireOp",EDGE,"E2.2.7.0")])],"isStart":false});
            var Q115;
            Q115=makeQuery(id+"F1.opExtrude","CAP_EDGE",EDGE,{"disambiguationData":[OSD([sQuery(id+"F0.wireOp",EDGE,"E3.0.3.2")])],"isStart":false});
            var Q116;
            Q116=makeQuery(id+"F1.opExtrude","CAP_EDGE",EDGE,{"disambiguationData":[OSD([sQuery(id+"F0.wireOp",EDGE,"E3.0.4.1")])],"isStart":false});
            var Q117;
            Q117=makeQuery(id+"F1.opExtrude","CAP_EDGE",EDGE,{"disambiguationData":[OSD([sQuery(id+"F0.wireOp",EDGE,"E3.0.4.5")])],"isStart":false});
            var Q118;
            Q118=makeQuery(id+"F1.opExtrude","CAP_EDGE",EDGE,{"disambiguationData":[OSD([sQuery(id+"F0.wireOp",EDGE,"E3.0.5.0")])],"isStart":false});
            var Q119;
            Q119=makeQuery(id+"F1.opExtrude","CAP_EDGE",EDGE,{"disambiguationData":[OSD([sQuery(id+"F0.wireOp",EDGE,"E3.0.5.4")])],"isStart":false});
            var Q120;
            Q120=makeQuery(id+"F1.opExtrude","CAP_EDGE",EDGE,{"disambiguationData":[OSD([sQuery(id+"F0.wireOp",EDGE,"E3.0.5.8")])],"isStart":false});
            var Q121;
            Q121=makeQuery(id+"F1.opExtrude","CAP_EDGE",EDGE,{"disambiguationData":[OSD([sQuery(id+"F0.wireOp",EDGE,"E3.0.6.3")])],"isStart":false});
            var Q122;
            Q122=makeQuery(id+"F1.opExtrude","CAP_EDGE",EDGE,{"disambiguationData":[OSD([sQuery(id+"F0.wireOp",EDGE,"E3.0.6.7")])],"isStart":false});
            var Q123;
            Q123=makeQuery(id+"F1.opExtrude","CAP_EDGE",EDGE,{"disambiguationData":[OSD([sQuery(id+"F0.wireOp",EDGE,"E3.0.7.2")])],"isStart":false});
            var Q124;
            Q124=makeQuery(id+"F1.opExtrude","CAP_EDGE",EDGE,{"disambiguationData":[OSD([sQuery(id+"F0.wireOp",EDGE,"E3.0.7.6")])],"isStart":false});
            var Q125;
            Q125=makeQuery(id+"F1.opExtrude","CAP_EDGE",EDGE,{"disambiguationData":[OSD([sQuery(id+"F0.wireOp",EDGE,"E2.0.5.1")])],"isStart":false});
            var Q126;
            Q126=makeQuery(id+"F1.opExtrude","CAP_EDGE",EDGE,{"disambiguationData":[OSD([sQuery(id+"F0.wireOp",EDGE,"E2.1.0.1")])],"isStart":false});
            var Q127;
            Q127=makeQuery(id+"F1.opExtrude","CAP_EDGE",EDGE,{"disambiguationData":[OSD([sQuery(id+"F0.wireOp",EDGE,"E2.1.4.1")])],"isStart":false});
            var Q128;
            Q128=makeQuery(id+"F1.opExtrude","CAP_EDGE",EDGE,{"disambiguationData":[OSD([sQuery(id+"F0.wireOp",EDGE,"E2.1.8.1")])],"isStart":false});
            var Q129;
            Q129=makeQuery(id+"F1.opExtrude","CAP_EDGE",EDGE,{"disambiguationData":[OSD([sQuery(id+"F0.wireOp",EDGE,"E2.2.3.1")])],"isStart":false});
            var Q130;
            Q130=makeQuery(id+"F1.opExtrude","CAP_EDGE",EDGE,{"disambiguationData":[OSD([sQuery(id+"F0.wireOp",EDGE,"E2.2.7.1")])],"isStart":false});
            var Q131;
            Q131=makeQuery(id+"F1.opExtrude","CAP_EDGE",EDGE,{"disambiguationData":[OSD([sQuery(id+"F0.wireOp",EDGE,"E3.2.3.2")])],"isStart":false});
            var Q132;
            Q132=makeQuery(id+"F1.opExtrude","CAP_EDGE",EDGE,{"disambiguationData":[OSD([sQuery(id+"F0.wireOp",EDGE,"E3.2.3.6")])],"isStart":false});
            var Q133;
            Q133=makeQuery(id+"F1.opExtrude","CAP_EDGE",EDGE,{"disambiguationData":[OSD([sQuery(id+"F0.wireOp",EDGE,"E3.2.4.1")])],"isStart":false});
            var Q134;
            Q134=makeQuery(id+"F1.opExtrude","CAP_EDGE",EDGE,{"disambiguationData":[OSD([sQuery(id+"F0.wireOp",EDGE,"E3.2.4.5")])],"isStart":false});
            var Q135;
            Q135=makeQuery(id+"F1.opExtrude","CAP_EDGE",EDGE,{"disambiguationData":[OSD([sQuery(id+"F0.wireOp",EDGE,"E3.2.5.0")])],"isStart":false});
            var Q136;
            Q136=makeQuery(id+"F1.opExtrude","CAP_EDGE",EDGE,{"disambiguationData":[OSD([sQuery(id+"F0.wireOp",EDGE,"E3.2.5.4")])],"isStart":false});
            var Q137;
            Q137=makeQuery(id+"F1.opExtrude","CAP_EDGE",EDGE,{"disambiguationData":[OSD([sQuery(id+"F0.wireOp",EDGE,"E3.2.5.8")])],"isStart":false});
            var Q138;
            Q138=makeQuery(id+"F1.opExtrude","CAP_EDGE",EDGE,{"disambiguationData":[OSD([sQuery(id+"F0.wireOp",EDGE,"E3.2.6.3")])],"isStart":false});
            var Q139;
            Q139=makeQuery(id+"F1.opExtrude","CAP_EDGE",EDGE,{"disambiguationData":[OSD([sQuery(id+"F0.wireOp",EDGE,"E3.2.6.7")])],"isStart":false});
            var Q140;
            Q140=makeQuery(id+"F1.opExtrude","CAP_EDGE",EDGE,{"disambiguationData":[OSD([sQuery(id+"F0.wireOp",EDGE,"E3.2.7.2")])],"isStart":false});
            var Q141;
            Q141=makeQuery(id+"F1.opExtrude","CAP_EDGE",EDGE,{"disambiguationData":[OSD([sQuery(id+"F0.wireOp",EDGE,"E3.2.7.6")])],"isStart":false});
            var Q142;
            Q142=makeQuery(id+"F1.opExtrude","CAP_EDGE",EDGE,{"disambiguationData":[OSD([sQuery(id+"F0.wireOp",EDGE,"E3.0.3.6")])],"isStart":false});
            var Q143;
            Q143=makeQuery(id+"F1.opExtrude","CAP_EDGE",EDGE,{"disambiguationData":[OSD([sQuery(id+"F0.wireOp",EDGE,"E2.0.2.1")])],"isStart":true});
            var Q144;
            Q144=makeQuery(id+"F1.opExtrude","CAP_EDGE",EDGE,{"disambiguationData":[OSD([sQuery(id+"F0.wireOp",EDGE,"E2.1.6.1")])],"isStart":true});
            var Q145;
            Q145=makeQuery(id+"F1.opExtrude","CAP_EDGE",EDGE,{"disambiguationData":[OSD([sQuery(id+"F0.wireOp",EDGE,"E0")])],"isStart":false});
            var Q146;
            Q146=makeQuery(id+"F1.opExtrude","CAP_EDGE",EDGE,{"disambiguationData":[OSD([sQuery(id+"F0.wireOp",EDGE,"E1")])],"isStart":true});
            var Q147;
            Q147=makeQuery(id+"F1.opExtrude","CAP_EDGE",EDGE,{"disambiguationData":[OSD([sQuery(id+"F0.wireOp",EDGE,"E2.0.1.0")])],"isStart":true});
            var Q148;
            Q148=makeQuery(id+"F1.opExtrude","CAP_EDGE",EDGE,{"disambiguationData":[OSD([sQuery(id+"F0.wireOp",EDGE,"E2.0.1.1")])],"isStart":true});
            var Q149;
            Q149=makeQuery(id+"F1.opExtrude","CAP_EDGE",EDGE,{"disambiguationData":[OSD([sQuery(id+"F0.wireOp",EDGE,"E2.0.2.0")])],"isStart":true});
            var Q150;
            Q150=makeQuery(id+"F1.opExtrude","CAP_EDGE",EDGE,{"disambiguationData":[OSD([sQuery(id+"F0.wireOp",EDGE,"E2.1.1.1")])],"isStart":true});
            var Q151;
            Q151=makeQuery(id+"F1.opExtrude","CAP_EDGE",EDGE,{"disambiguationData":[OSD([sQuery(id+"F0.wireOp",EDGE,"E2.1.5.1")])],"isStart":true});
            var Q152;
            Q152=makeQuery(id+"F1.opExtrude","CAP_EDGE",EDGE,{"disambiguationData":[OSD([sQuery(id+"F0.wireOp",EDGE,"E2.2.0.1")])],"isStart":true});
            var Q153;
            Q153=makeQuery(id+"F1.opExtrude","CAP_EDGE",EDGE,{"disambiguationData":[OSD([sQuery(id+"F0.wireOp",EDGE,"E2.2.4.1")])],"isStart":true});
            var Q154;
            Q154=makeQuery(id+"F1.opExtrude","CAP_EDGE",EDGE,{"disambiguationData":[OSD([sQuery(id+"F0.wireOp",EDGE,"E2.2.8.1")])],"isStart":true});
            var Q155;
            Q155=makeQuery(id+"F1.opExtrude","CAP_EDGE",EDGE,{"disambiguationData":[OSD([sQuery(id+"F0.wireOp",EDGE,"E3.2.3.3")])],"isStart":true});
            var Q156;
            Q156=makeQuery(id+"F1.opExtrude","CAP_EDGE",EDGE,{"disambiguationData":[OSD([sQuery(id+"F0.wireOp",EDGE,"E3.2.3.7")])],"isStart":true});
            var Q157;
            Q157=makeQuery(id+"F1.opExtrude","CAP_EDGE",EDGE,{"disambiguationData":[OSD([sQuery(id+"F0.wireOp",EDGE,"E3.2.4.2")])],"isStart":true});
            var Q158;
            Q158=makeQuery(id+"F1.opExtrude","CAP_EDGE",EDGE,{"disambiguationData":[OSD([sQuery(id+"F0.wireOp",EDGE,"E3.2.4.6")])],"isStart":true});
            var Q159;
            Q159=makeQuery(id+"F1.opExtrude","CAP_EDGE",EDGE,{"disambiguationData":[OSD([sQuery(id+"F0.wireOp",EDGE,"E3.2.5.1")])],"isStart":true});
            var Q160;
            Q160=makeQuery(id+"F1.opExtrude","CAP_EDGE",EDGE,{"disambiguationData":[OSD([sQuery(id+"F0.wireOp",EDGE,"E3.2.5.5")])],"isStart":true});
            var Q161;
            Q161=makeQuery(id+"F1.opExtrude","CAP_EDGE",EDGE,{"disambiguationData":[OSD([sQuery(id+"F0.wireOp",EDGE,"E3.2.6.0")])],"isStart":true});
            var Q162;
            Q162=makeQuery(id+"F1.opExtrude","CAP_EDGE",EDGE,{"disambiguationData":[OSD([sQuery(id+"F0.wireOp",EDGE,"E3.2.6.4")])],"isStart":true});
            var Q163;
            Q163=makeQuery(id+"F1.opExtrude","CAP_EDGE",EDGE,{"disambiguationData":[OSD([sQuery(id+"F0.wireOp",EDGE,"E3.2.6.8")])],"isStart":true});
            var Q164;
            Q164=makeQuery(id+"F1.opExtrude","CAP_EDGE",EDGE,{"disambiguationData":[OSD([sQuery(id+"F0.wireOp",EDGE,"E3.2.7.3")])],"isStart":true});
            var Q165;
            Q165=makeQuery(id+"F1.opExtrude","CAP_EDGE",EDGE,{"disambiguationData":[OSD([sQuery(id+"F0.wireOp",EDGE,"E3.2.7.7")])],"isStart":true});
            var Q166;
            Q166=makeQuery(id+"F1.opExtrude","CAP_EDGE",EDGE,{"disambiguationData":[OSD([sQuery(id+"F0.wireOp",EDGE,"E2.2.6.1")])],"isStart":true});
            var Q167;
            Q167=makeQuery(id+"F1.opExtrude","CAP_EDGE",EDGE,{"disambiguationData":[OSD([sQuery(id+"F0.wireOp",EDGE,"E2.0.3.0")])],"isStart":true});
            var Q168;
            Q168=makeQuery(id+"F1.opExtrude","CAP_EDGE",EDGE,{"disambiguationData":[OSD([sQuery(id+"F0.wireOp",EDGE,"E2.0.7.0")])],"isStart":true});
            var Q169;
            Q169=makeQuery(id+"F1.opExtrude","CAP_EDGE",EDGE,{"disambiguationData":[OSD([sQuery(id+"F0.wireOp",EDGE,"E2.1.2.0")])],"isStart":true});
            var Q170;
            Q170=makeQuery(id+"F1.opExtrude","CAP_EDGE",EDGE,{"disambiguationData":[OSD([sQuery(id+"F0.wireOp",EDGE,"E2.1.6.0")])],"isStart":true});
            var Q171;
            Q171=makeQuery(id+"F1.opExtrude","CAP_EDGE",EDGE,{"disambiguationData":[OSD([sQuery(id+"F0.wireOp",EDGE,"E2.2.1.0")])],"isStart":true});
            var Q172;
            Q172=makeQuery(id+"F1.opExtrude","CAP_EDGE",EDGE,{"disambiguationData":[OSD([sQuery(id+"F0.wireOp",EDGE,"E2.2.5.0")])],"isStart":true});
            var Q173;
            Q173=makeQuery(id+"F1.opExtrude","CAP_EDGE",EDGE,{"disambiguationData":[OSD([sQuery(id+"F0.wireOp",EDGE,"E3.0.3.0")])],"isStart":true});
            var Q174;
            Q174=makeQuery(id+"F1.opExtrude","CAP_EDGE",EDGE,{"disambiguationData":[OSD([sQuery(id+"F0.wireOp",EDGE,"E3.0.3.4")])],"isStart":true});
            var Q175;
            Q175=makeQuery(id+"F1.opExtrude","CAP_EDGE",EDGE,{"disambiguationData":[OSD([sQuery(id+"F0.wireOp",EDGE,"E3.0.3.8")])],"isStart":true});
            var Q176;
            Q176=makeQuery(id+"F1.opExtrude","CAP_EDGE",EDGE,{"disambiguationData":[OSD([sQuery(id+"F0.wireOp",EDGE,"E3.0.4.3")])],"isStart":true});
            var Q177;
            Q177=makeQuery(id+"F1.opExtrude","CAP_EDGE",EDGE,{"disambiguationData":[OSD([sQuery(id+"F0.wireOp",EDGE,"E3.0.4.7")])],"isStart":true});
            var Q178;
            Q178=makeQuery(id+"F1.opExtrude","CAP_EDGE",EDGE,{"disambiguationData":[OSD([sQuery(id+"F0.wireOp",EDGE,"E3.0.5.2")])],"isStart":true});
            var Q179;
            Q179=makeQuery(id+"F1.opExtrude","CAP_EDGE",EDGE,{"disambiguationData":[OSD([sQuery(id+"F0.wireOp",EDGE,"E3.0.5.6")])],"isStart":true});
            var Q180;
            Q180=makeQuery(id+"F1.opExtrude","CAP_EDGE",EDGE,{"disambiguationData":[OSD([sQuery(id+"F0.wireOp",EDGE,"E3.0.6.1")])],"isStart":true});
            var Q181;
            Q181=makeQuery(id+"F1.opExtrude","CAP_EDGE",EDGE,{"disambiguationData":[OSD([sQuery(id+"F0.wireOp",EDGE,"E3.0.6.5")])],"isStart":true});
            var Q182;
            Q182=makeQuery(id+"F1.opExtrude","CAP_EDGE",EDGE,{"disambiguationData":[OSD([sQuery(id+"F0.wireOp",EDGE,"E3.0.7.0")])],"isStart":true});
            var Q183;
            Q183=makeQuery(id+"F1.opExtrude","CAP_EDGE",EDGE,{"disambiguationData":[OSD([sQuery(id+"F0.wireOp",EDGE,"E3.0.7.4")])],"isStart":true});
            var Q184;
            Q184=makeQuery(id+"F1.opExtrude","CAP_EDGE",EDGE,{"disambiguationData":[OSD([sQuery(id+"F0.wireOp",EDGE,"E3.0.7.8")])],"isStart":true});
            var Q185;
            Q185=makeQuery(id+"F1.opExtrude","CAP_EDGE",EDGE,{"disambiguationData":[OSD([sQuery(id+"F0.wireOp",EDGE,"E2.0.3.1")])],"isStart":true});
            var Q186;
            Q186=makeQuery(id+"F1.opExtrude","CAP_EDGE",EDGE,{"disambiguationData":[OSD([sQuery(id+"F0.wireOp",EDGE,"E2.0.7.1")])],"isStart":true});
            var Q187;
            Q187=makeQuery(id+"F1.opExtrude","CAP_EDGE",EDGE,{"disambiguationData":[OSD([sQuery(id+"F0.wireOp",EDGE,"E2.1.2.1")])],"isStart":true});
            var Q188;
            Q188=makeQuery(id+"F1.opExtrude","CAP_EDGE",EDGE,{"disambiguationData":[OSD([sQuery(id+"F0.wireOp",EDGE,"E2.2.1.1")])],"isStart":true});
            var Q189;
            Q189=makeQuery(id+"F1.opExtrude","CAP_EDGE",EDGE,{"disambiguationData":[OSD([sQuery(id+"F0.wireOp",EDGE,"E2.2.5.1")])],"isStart":true});
            var Q190;
            Q190=makeQuery(id+"F1.opExtrude","CAP_EDGE",EDGE,{"disambiguationData":[OSD([sQuery(id+"F0.wireOp",EDGE,"E3.2.3.0")])],"isStart":true});
            var Q191;
            Q191=makeQuery(id+"F1.opExtrude","CAP_EDGE",EDGE,{"disambiguationData":[OSD([sQuery(id+"F0.wireOp",EDGE,"E3.2.3.4")])],"isStart":true});
            var Q192;
            Q192=makeQuery(id+"F1.opExtrude","CAP_EDGE",EDGE,{"disambiguationData":[OSD([sQuery(id+"F0.wireOp",EDGE,"E3.2.3.8")])],"isStart":true});
            var Q193;
            Q193=makeQuery(id+"F1.opExtrude","CAP_EDGE",EDGE,{"disambiguationData":[OSD([sQuery(id+"F0.wireOp",EDGE,"E3.2.4.3")])],"isStart":true});
            var Q194;
            Q194=makeQuery(id+"F1.opExtrude","CAP_EDGE",EDGE,{"disambiguationData":[OSD([sQuery(id+"F0.wireOp",EDGE,"E3.2.4.7")])],"isStart":true});
            var Q195;
            Q195=makeQuery(id+"F1.opExtrude","CAP_EDGE",EDGE,{"disambiguationData":[OSD([sQuery(id+"F0.wireOp",EDGE,"E3.2.5.2")])],"isStart":true});
            var Q196;
            Q196=makeQuery(id+"F1.opExtrude","CAP_EDGE",EDGE,{"disambiguationData":[OSD([sQuery(id+"F0.wireOp",EDGE,"E3.2.5.6")])],"isStart":true});
            var Q197;
            Q197=makeQuery(id+"F1.opExtrude","CAP_EDGE",EDGE,{"disambiguationData":[OSD([sQuery(id+"F0.wireOp",EDGE,"E3.2.6.1")])],"isStart":true});
            var Q198;
            Q198=makeQuery(id+"F1.opExtrude","CAP_EDGE",EDGE,{"disambiguationData":[OSD([sQuery(id+"F0.wireOp",EDGE,"E3.2.6.5")])],"isStart":true});
            var Q199;
            Q199=makeQuery(id+"F1.opExtrude","CAP_EDGE",EDGE,{"disambiguationData":[OSD([sQuery(id+"F0.wireOp",EDGE,"E3.2.7.0")])],"isStart":true});
            var Q200;
            Q200=makeQuery(id+"F1.opExtrude","CAP_EDGE",EDGE,{"disambiguationData":[OSD([sQuery(id+"F0.wireOp",EDGE,"E3.2.7.4")])],"isStart":true});
            var Q201;
            Q201=makeQuery(id+"F1.opExtrude","CAP_EDGE",EDGE,{"disambiguationData":[OSD([sQuery(id+"F0.wireOp",EDGE,"E3.2.7.8")])],"isStart":true});
            var Q202;
            Q202=makeQuery(id+"F1.opExtrude","CAP_EDGE",EDGE,{"disambiguationData":[OSD([sQuery(id+"F0.wireOp",EDGE,"E3.2.3.6")])],"isStart":true});
            var Q203;
            Q203=makeQuery(id+"F1.opExtrude","CAP_EDGE",EDGE,{"disambiguationData":[OSD([sQuery(id+"F0.wireOp",EDGE,"E2.0.8.1")])],"isStart":true});
            var Q204;
            Q204=makeQuery(id+"F1.opExtrude","CAP_EDGE",EDGE,{"disambiguationData":[OSD([sQuery(id+"F0.wireOp",EDGE,"E2.0.4.0")])],"isStart":true});
            var Q205;
            Q205=makeQuery(id+"F1.opExtrude","CAP_EDGE",EDGE,{"disambiguationData":[OSD([sQuery(id+"F0.wireOp",EDGE,"E2.1.3.0")])],"isStart":true});
            var Q206;
            Q206=makeQuery(id+"F1.opExtrude","CAP_EDGE",EDGE,{"disambiguationData":[OSD([sQuery(id+"F0.wireOp",EDGE,"E2.1.7.0")])],"isStart":true});
            var Q207;
            Q207=makeQuery(id+"F1.opExtrude","CAP_EDGE",EDGE,{"disambiguationData":[OSD([sQuery(id+"F0.wireOp",EDGE,"E2.2.2.0")])],"isStart":true});
            var Q208;
            Q208=makeQuery(id+"F1.opExtrude","CAP_EDGE",EDGE,{"disambiguationData":[OSD([sQuery(id+"F0.wireOp",EDGE,"E2.2.6.0")])],"isStart":true});
            var Q209;
            Q209=makeQuery(id+"F1.opExtrude","CAP_EDGE",EDGE,{"disambiguationData":[OSD([sQuery(id+"F0.wireOp",EDGE,"E3.0.3.1")])],"isStart":true});
            var Q210;
            Q210=makeQuery(id+"F1.opExtrude","CAP_EDGE",EDGE,{"disambiguationData":[OSD([sQuery(id+"F0.wireOp",EDGE,"E3.0.3.5")])],"isStart":true});
            var Q211;
            Q211=makeQuery(id+"F1.opExtrude","CAP_EDGE",EDGE,{"disambiguationData":[OSD([sQuery(id+"F0.wireOp",EDGE,"E3.0.4.0")])],"isStart":true});
            var Q212;
            Q212=makeQuery(id+"F1.opExtrude","CAP_EDGE",EDGE,{"disambiguationData":[OSD([sQuery(id+"F0.wireOp",EDGE,"E3.0.4.4")])],"isStart":true});
            var Q213;
            Q213=makeQuery(id+"F1.opExtrude","CAP_EDGE",EDGE,{"disambiguationData":[OSD([sQuery(id+"F0.wireOp",EDGE,"E3.0.4.8")])],"isStart":true});
            var Q214;
            Q214=makeQuery(id+"F1.opExtrude","CAP_EDGE",EDGE,{"disambiguationData":[OSD([sQuery(id+"F0.wireOp",EDGE,"E3.0.5.3")])],"isStart":true});
            var Q215;
            Q215=makeQuery(id+"F1.opExtrude","CAP_EDGE",EDGE,{"disambiguationData":[OSD([sQuery(id+"F0.wireOp",EDGE,"E3.0.5.7")])],"isStart":true});
            var Q216;
            Q216=makeQuery(id+"F1.opExtrude","CAP_EDGE",EDGE,{"disambiguationData":[OSD([sQuery(id+"F0.wireOp",EDGE,"E3.0.6.2")])],"isStart":true});
            var Q217;
            Q217=makeQuery(id+"F1.opExtrude","CAP_EDGE",EDGE,{"disambiguationData":[OSD([sQuery(id+"F0.wireOp",EDGE,"E3.0.6.6")])],"isStart":true});
            var Q218;
            Q218=makeQuery(id+"F1.opExtrude","CAP_EDGE",EDGE,{"disambiguationData":[OSD([sQuery(id+"F0.wireOp",EDGE,"E3.0.7.1")])],"isStart":true});
            var Q219;
            Q219=makeQuery(id+"F1.opExtrude","CAP_EDGE",EDGE,{"disambiguationData":[OSD([sQuery(id+"F0.wireOp",EDGE,"E3.0.7.5")])],"isStart":true});
            var Q220;
            Q220=makeQuery(id+"F1.opExtrude","CAP_EDGE",EDGE,{"disambiguationData":[OSD([sQuery(id+"F0.wireOp",EDGE,"E2.0.4.1")])],"isStart":true});
            var Q221;
            Q221=makeQuery(id+"F1.opExtrude","CAP_EDGE",EDGE,{"disambiguationData":[OSD([sQuery(id+"F0.wireOp",EDGE,"E2.0.6.1")])],"isStart":true});
            var Q222;
            Q222=makeQuery(id+"F1.opExtrude","CAP_EDGE",EDGE,{"disambiguationData":[OSD([sQuery(id+"F0.wireOp",EDGE,"E2.1.3.1")])],"isStart":true});
            var Q223;
            Q223=makeQuery(id+"F1.opExtrude","CAP_EDGE",EDGE,{"disambiguationData":[OSD([sQuery(id+"F0.wireOp",EDGE,"E2.1.7.1")])],"isStart":true});
            var Q224;
            Q224=makeQuery(id+"F1.opExtrude","CAP_EDGE",EDGE,{"disambiguationData":[OSD([sQuery(id+"F0.wireOp",EDGE,"E2.2.2.1")])],"isStart":true});
            var Q225;
            Q225=makeQuery(id+"F1.opExtrude","CAP_EDGE",EDGE,{"disambiguationData":[OSD([sQuery(id+"F0.wireOp",EDGE,"E2.0.8.0")])],"isStart":true});
            var Q226;
            Q226=makeQuery(id+"F1.opExtrude","CAP_EDGE",EDGE,{"disambiguationData":[OSD([sQuery(id+"F0.wireOp",EDGE,"E3.2.3.1")])],"isStart":true});
            var Q227;
            Q227=makeQuery(id+"F1.opExtrude","CAP_EDGE",EDGE,{"disambiguationData":[OSD([sQuery(id+"F0.wireOp",EDGE,"E3.2.3.5")])],"isStart":true});
            var Q228;
            Q228=makeQuery(id+"F1.opExtrude","CAP_EDGE",EDGE,{"disambiguationData":[OSD([sQuery(id+"F0.wireOp",EDGE,"E3.2.4.0")])],"isStart":true});
            var Q229;
            Q229=makeQuery(id+"F1.opExtrude","CAP_EDGE",EDGE,{"disambiguationData":[OSD([sQuery(id+"F0.wireOp",EDGE,"E3.2.4.4")])],"isStart":true});
            var Q230;
            Q230=makeQuery(id+"F1.opExtrude","CAP_EDGE",EDGE,{"disambiguationData":[OSD([sQuery(id+"F0.wireOp",EDGE,"E3.2.4.8")])],"isStart":true});
            var Q231;
            Q231=makeQuery(id+"F1.opExtrude","CAP_EDGE",EDGE,{"disambiguationData":[OSD([sQuery(id+"F0.wireOp",EDGE,"E3.2.5.3")])],"isStart":true});
            var Q232;
            Q232=makeQuery(id+"F1.opExtrude","CAP_EDGE",EDGE,{"disambiguationData":[OSD([sQuery(id+"F0.wireOp",EDGE,"E3.2.5.7")])],"isStart":true});
            var Q233;
            Q233=makeQuery(id+"F1.opExtrude","CAP_EDGE",EDGE,{"disambiguationData":[OSD([sQuery(id+"F0.wireOp",EDGE,"E3.2.6.2")])],"isStart":true});
            var Q234;
            Q234=makeQuery(id+"F1.opExtrude","CAP_EDGE",EDGE,{"disambiguationData":[OSD([sQuery(id+"F0.wireOp",EDGE,"E3.2.6.6")])],"isStart":true});
            var Q235;
            Q235=makeQuery(id+"F1.opExtrude","CAP_EDGE",EDGE,{"disambiguationData":[OSD([sQuery(id+"F0.wireOp",EDGE,"E3.2.7.1")])],"isStart":true});
            var Q236;
            Q236=makeQuery(id+"F1.opExtrude","CAP_EDGE",EDGE,{"disambiguationData":[OSD([sQuery(id+"F0.wireOp",EDGE,"E3.2.7.5")])],"isStart":true});
            var Q237;
            Q237=makeQuery(id+"F1.opExtrude","CAP_EDGE",EDGE,{"disambiguationData":[OSD([sQuery(id+"F0.wireOp",EDGE,"E2.0.5.0")])],"isStart":true});
            var Q238;
            Q238=makeQuery(id+"F1.opExtrude","CAP_EDGE",EDGE,{"disambiguationData":[OSD([sQuery(id+"F0.wireOp",EDGE,"E2.1.0.0")])],"isStart":true});
            var Q239;
            Q239=makeQuery(id+"F1.opExtrude","CAP_EDGE",EDGE,{"disambiguationData":[OSD([sQuery(id+"F0.wireOp",EDGE,"E2.1.4.0")])],"isStart":true});
            var Q240;
            Q240=makeQuery(id+"F1.opExtrude","CAP_EDGE",EDGE,{"disambiguationData":[OSD([sQuery(id+"F0.wireOp",EDGE,"E2.1.8.0")])],"isStart":true});
            var Q241;
            Q241=makeQuery(id+"F1.opExtrude","CAP_EDGE",EDGE,{"disambiguationData":[OSD([sQuery(id+"F0.wireOp",EDGE,"E2.2.3.0")])],"isStart":true});
            var Q242;
            Q242=makeQuery(id+"F1.opExtrude","CAP_EDGE",EDGE,{"disambiguationData":[OSD([sQuery(id+"F0.wireOp",EDGE,"E2.2.7.0")])],"isStart":true});
            var Q243;
            Q243=makeQuery(id+"F1.opExtrude","CAP_EDGE",EDGE,{"disambiguationData":[OSD([sQuery(id+"F0.wireOp",EDGE,"E3.0.3.2")])],"isStart":true});
            var Q244;
            Q244=makeQuery(id+"F1.opExtrude","CAP_EDGE",EDGE,{"disambiguationData":[OSD([sQuery(id+"F0.wireOp",EDGE,"E3.0.3.6")])],"isStart":true});
            var Q245;
            Q245=makeQuery(id+"F1.opExtrude","CAP_EDGE",EDGE,{"disambiguationData":[OSD([sQuery(id+"F0.wireOp",EDGE,"E3.0.4.1")])],"isStart":true});
            var Q246;
            Q246=makeQuery(id+"F1.opExtrude","CAP_EDGE",EDGE,{"disambiguationData":[OSD([sQuery(id+"F0.wireOp",EDGE,"E3.0.4.5")])],"isStart":true});
            var Q247;
            Q247=makeQuery(id+"F1.opExtrude","CAP_EDGE",EDGE,{"disambiguationData":[OSD([sQuery(id+"F0.wireOp",EDGE,"E3.0.5.0")])],"isStart":true});
            var Q248;
            Q248=makeQuery(id+"F1.opExtrude","CAP_EDGE",EDGE,{"disambiguationData":[OSD([sQuery(id+"F0.wireOp",EDGE,"E3.0.5.4")])],"isStart":true});
            var Q249;
            Q249=makeQuery(id+"F1.opExtrude","CAP_EDGE",EDGE,{"disambiguationData":[OSD([sQuery(id+"F0.wireOp",EDGE,"E3.0.5.8")])],"isStart":true});
            var Q250;
            Q250=makeQuery(id+"F1.opExtrude","CAP_EDGE",EDGE,{"disambiguationData":[OSD([sQuery(id+"F0.wireOp",EDGE,"E3.0.6.3")])],"isStart":true});
            var Q251;
            Q251=makeQuery(id+"F1.opExtrude","CAP_EDGE",EDGE,{"disambiguationData":[OSD([sQuery(id+"F0.wireOp",EDGE,"E3.0.6.7")])],"isStart":true});
            var Q252;
            Q252=makeQuery(id+"F1.opExtrude","CAP_EDGE",EDGE,{"disambiguationData":[OSD([sQuery(id+"F0.wireOp",EDGE,"E3.0.7.2")])],"isStart":true});
            var Q253;
            Q253=makeQuery(id+"F1.opExtrude","CAP_EDGE",EDGE,{"disambiguationData":[OSD([sQuery(id+"F0.wireOp",EDGE,"E3.0.7.6")])],"isStart":true});
            var Q254;
            Q254=makeQuery(id+"F1.opExtrude","CAP_EDGE",EDGE,{"disambiguationData":[OSD([sQuery(id+"F0.wireOp",EDGE,"E2.0.5.1")])],"isStart":true});
            var Q255;
            Q255=makeQuery(id+"F1.opExtrude","CAP_EDGE",EDGE,{"disambiguationData":[OSD([sQuery(id+"F0.wireOp",EDGE,"E2.1.0.1")])],"isStart":true});
            var Q256;
            Q256=makeQuery(id+"F1.opExtrude","CAP_EDGE",EDGE,{"disambiguationData":[OSD([sQuery(id+"F0.wireOp",EDGE,"E2.1.4.1")])],"isStart":true});
            var Q257;
            Q257=makeQuery(id+"F1.opExtrude","CAP_EDGE",EDGE,{"disambiguationData":[OSD([sQuery(id+"F0.wireOp",EDGE,"E2.1.8.1")])],"isStart":true});
            var Q258;
            Q258=makeQuery(id+"F1.opExtrude","CAP_EDGE",EDGE,{"disambiguationData":[OSD([sQuery(id+"F0.wireOp",EDGE,"E2.2.3.1")])],"isStart":true});
            var Q259;
            Q259=makeQuery(id+"F1.opExtrude","CAP_EDGE",EDGE,{"disambiguationData":[OSD([sQuery(id+"F0.wireOp",EDGE,"E2.2.7.1")])],"isStart":true});
            var Q260;
            Q260=makeQuery(id+"F1.opExtrude","CAP_EDGE",EDGE,{"disambiguationData":[OSD([sQuery(id+"F0.wireOp",EDGE,"E3.2.3.2")])],"isStart":true});
            var Q261;
            Q261=makeQuery(id+"F1.opExtrude","CAP_EDGE",EDGE,{"disambiguationData":[OSD([sQuery(id+"F0.wireOp",EDGE,"E3.2.4.1")])],"isStart":true});
            var Q262;
            Q262=makeQuery(id+"F1.opExtrude","CAP_EDGE",EDGE,{"disambiguationData":[OSD([sQuery(id+"F0.wireOp",EDGE,"E3.2.4.5")])],"isStart":true});
            var Q263;
            Q263=makeQuery(id+"F1.opExtrude","CAP_EDGE",EDGE,{"disambiguationData":[OSD([sQuery(id+"F0.wireOp",EDGE,"E3.2.5.0")])],"isStart":true});
            var Q264;
            Q264=makeQuery(id+"F1.opExtrude","CAP_EDGE",EDGE,{"disambiguationData":[OSD([sQuery(id+"F0.wireOp",EDGE,"E3.2.5.4")])],"isStart":true});
            var Q265;
            Q265=makeQuery(id+"F1.opExtrude","CAP_EDGE",EDGE,{"disambiguationData":[OSD([sQuery(id+"F0.wireOp",EDGE,"E3.2.5.8")])],"isStart":true});
            var Q266;
            Q266=makeQuery(id+"F1.opExtrude","CAP_EDGE",EDGE,{"disambiguationData":[OSD([sQuery(id+"F0.wireOp",EDGE,"E3.2.6.3")])],"isStart":true});
            var Q267;
            Q267=makeQuery(id+"F1.opExtrude","CAP_EDGE",EDGE,{"disambiguationData":[OSD([sQuery(id+"F0.wireOp",EDGE,"E3.2.6.7")])],"isStart":true});
            var Q268;
            Q268=makeQuery(id+"F1.opExtrude","CAP_EDGE",EDGE,{"disambiguationData":[OSD([sQuery(id+"F0.wireOp",EDGE,"E3.2.7.2")])],"isStart":true});
            var Q269;
            Q269=makeQuery(id+"F1.opExtrude","CAP_EDGE",EDGE,{"disambiguationData":[OSD([sQuery(id+"F0.wireOp",EDGE,"E3.2.7.6")])],"isStart":true});
            var Q270;
            Q270=makeQuery(id+"F1.opExtrude","CAP_EDGE",EDGE,{"disambiguationData":[OSD([sQuery(id+"F0.wireOp",EDGE,"E2.0.6.0")])],"isStart":true});
            var Q271;
            Q271=makeQuery(id+"F1.opExtrude","CAP_EDGE",EDGE,{"disambiguationData":[OSD([sQuery(id+"F0.wireOp",EDGE,"E2.1.1.0")])],"isStart":true});
            var Q272;
            Q272=makeQuery(id+"F1.opExtrude","CAP_EDGE",EDGE,{"disambiguationData":[OSD([sQuery(id+"F0.wireOp",EDGE,"E2.1.5.0")])],"isStart":true});
            var Q273;
            Q273=makeQuery(id+"F1.opExtrude","CAP_EDGE",EDGE,{"disambiguationData":[OSD([sQuery(id+"F0.wireOp",EDGE,"E2.2.0.0")])],"isStart":true});
            var Q274;
            Q274=makeQuery(id+"F1.opExtrude","CAP_EDGE",EDGE,{"disambiguationData":[OSD([sQuery(id+"F0.wireOp",EDGE,"E2.2.4.0")])],"isStart":true});
            var Q275;
            Q275=makeQuery(id+"F1.opExtrude","CAP_EDGE",EDGE,{"disambiguationData":[OSD([sQuery(id+"F0.wireOp",EDGE,"E2.2.8.0")])],"isStart":true});
            var Q276;
            Q276=makeQuery(id+"F1.opExtrude","CAP_EDGE",EDGE,{"disambiguationData":[OSD([sQuery(id+"F0.wireOp",EDGE,"E3.0.3.3")])],"isStart":true});
            var Q277;
            Q277=makeQuery(id+"F1.opExtrude","CAP_EDGE",EDGE,{"disambiguationData":[OSD([sQuery(id+"F0.wireOp",EDGE,"E3.0.3.7")])],"isStart":true});
            var Q278;
            Q278=makeQuery(id+"F1.opExtrude","CAP_EDGE",EDGE,{"disambiguationData":[OSD([sQuery(id+"F0.wireOp",EDGE,"E3.0.4.2")])],"isStart":true});
            var Q279;
            Q279=makeQuery(id+"F1.opExtrude","CAP_EDGE",EDGE,{"disambiguationData":[OSD([sQuery(id+"F0.wireOp",EDGE,"E3.0.4.6")])],"isStart":true});
            var Q280;
            Q280=makeQuery(id+"F1.opExtrude","CAP_EDGE",EDGE,{"disambiguationData":[OSD([sQuery(id+"F0.wireOp",EDGE,"E3.0.5.1")])],"isStart":true});
            var Q281;
            Q281=makeQuery(id+"F1.opExtrude","CAP_EDGE",EDGE,{"disambiguationData":[OSD([sQuery(id+"F0.wireOp",EDGE,"E3.0.5.5")])],"isStart":true});
            var Q282;
            Q282=makeQuery(id+"F1.opExtrude","CAP_EDGE",EDGE,{"disambiguationData":[OSD([sQuery(id+"F0.wireOp",EDGE,"E3.0.6.0")])],"isStart":true});
            var Q283;
            Q283=makeQuery(id+"F1.opExtrude","CAP_EDGE",EDGE,{"disambiguationData":[OSD([sQuery(id+"F0.wireOp",EDGE,"E3.0.6.4")])],"isStart":true});
            var Q284;
            Q284=makeQuery(id+"F1.opExtrude","CAP_EDGE",EDGE,{"disambiguationData":[OSD([sQuery(id+"F0.wireOp",EDGE,"E3.0.6.8")])],"isStart":true});
            var Q285;
            Q285=makeQuery(id+"F1.opExtrude","CAP_EDGE",EDGE,{"disambiguationData":[OSD([sQuery(id+"F0.wireOp",EDGE,"E3.0.7.3")])],"isStart":true});
            var Q286;
            Q286=makeQuery(id+"F1.opExtrude","CAP_EDGE",EDGE,{"disambiguationData":[OSD([sQuery(id+"F0.wireOp",EDGE,"E3.0.7.7")])],"isStart":true});
            var Q287;
            Q287=makeQuery(id+"F1.opExtrude","CAP_EDGE",EDGE,{"disambiguationData":[OSD([sQuery(id+"F0.wireOp",EDGE,"E0")])],"isStart":true});
            fillet(context, id + "F2", {"entities" : qUnion([Q0, Q1, Q2, Q3, Q4, Q5, Q6, Q7, Q8, Q9, Q10, Q11, Q12, Q13, Q14, Q15, Q16, Q17, Q18, Q19, Q20, Q21, Q22, Q23, Q24, Q25, Q26, Q27, Q28, Q29, Q30, Q31, Q32, Q33, Q34, Q35, Q36, Q37, Q38, Q39, Q40, Q41, Q42, Q43, Q44, Q45, Q46, Q47, Q48, Q49, Q50, Q51, Q52, Q53, Q54, Q55, Q56, Q57, Q58, Q59, Q60, Q61, Q62, Q63, Q64, Q65, Q66, Q67, Q68, Q69, Q70, Q71, Q72, Q73, Q74, Q75, Q76, Q77, Q78, Q79, Q80, Q81, Q82, Q83, Q84, Q85, Q86, Q87, Q88, Q89, Q90, Q91, Q92, Q93, Q94, Q95, Q96, Q97, Q98, Q99, Q100, Q101, Q102, Q103, Q104, Q105, Q106, Q107, Q108, Q109, Q110, Q111, Q112, Q113, Q114, Q115, Q116, Q117, Q118, Q119, Q120, Q121, Q122, Q123, Q124, Q125, Q126, Q127, Q128, Q129, Q130, Q131, Q132, Q133, Q134, Q135, Q136, Q137, Q138, Q139, Q140, Q141, Q142, Q143, Q144, Q145, Q146, Q147, Q148, Q149, Q150, Q151, Q152, Q153, Q154, Q155, Q156, Q157, Q158, Q159, Q160, Q161, Q162, Q163, Q164, Q165, Q166, Q167, Q168, Q169, Q170, Q171, Q172, Q173, Q174, Q175, Q176, Q177, Q178, Q179, Q180, Q181, Q182, Q183, Q184, Q185, Q186, Q187, Q188, Q189, Q190, Q191, Q192, Q193, Q194, Q195, Q196, Q197, Q198, Q199, Q200, Q201, Q202, Q203, Q204, Q205, Q206, Q207, Q208, Q209, Q210, Q211, Q212, Q213, Q214, Q215, Q216, Q217, Q218, Q219, Q220, Q221, Q222, Q223, Q224, Q225, Q226, Q227, Q228, Q229, Q230, Q231, Q232, Q233, Q234, Q235, Q236, Q237, Q238, Q239, Q240, Q241, Q242, Q243, Q244, Q245, Q246, Q247, Q248, Q249, Q250, Q251, Q252, Q253, Q254, Q255, Q256, Q257, Q258, Q259, Q260, Q261, Q262, Q263, Q264, Q265, Q266, Q267, Q268, Q269, Q270, Q271, Q272, Q273, Q274, Q275, Q276, Q277, Q278, Q279, Q280, Q281, Q282, Q283, Q284, Q285, Q286, Q287]), "radius" : 0.5 * mm, "tangentPropagation" : true, "allowEdgeOverflow" : false});
        }
    });
